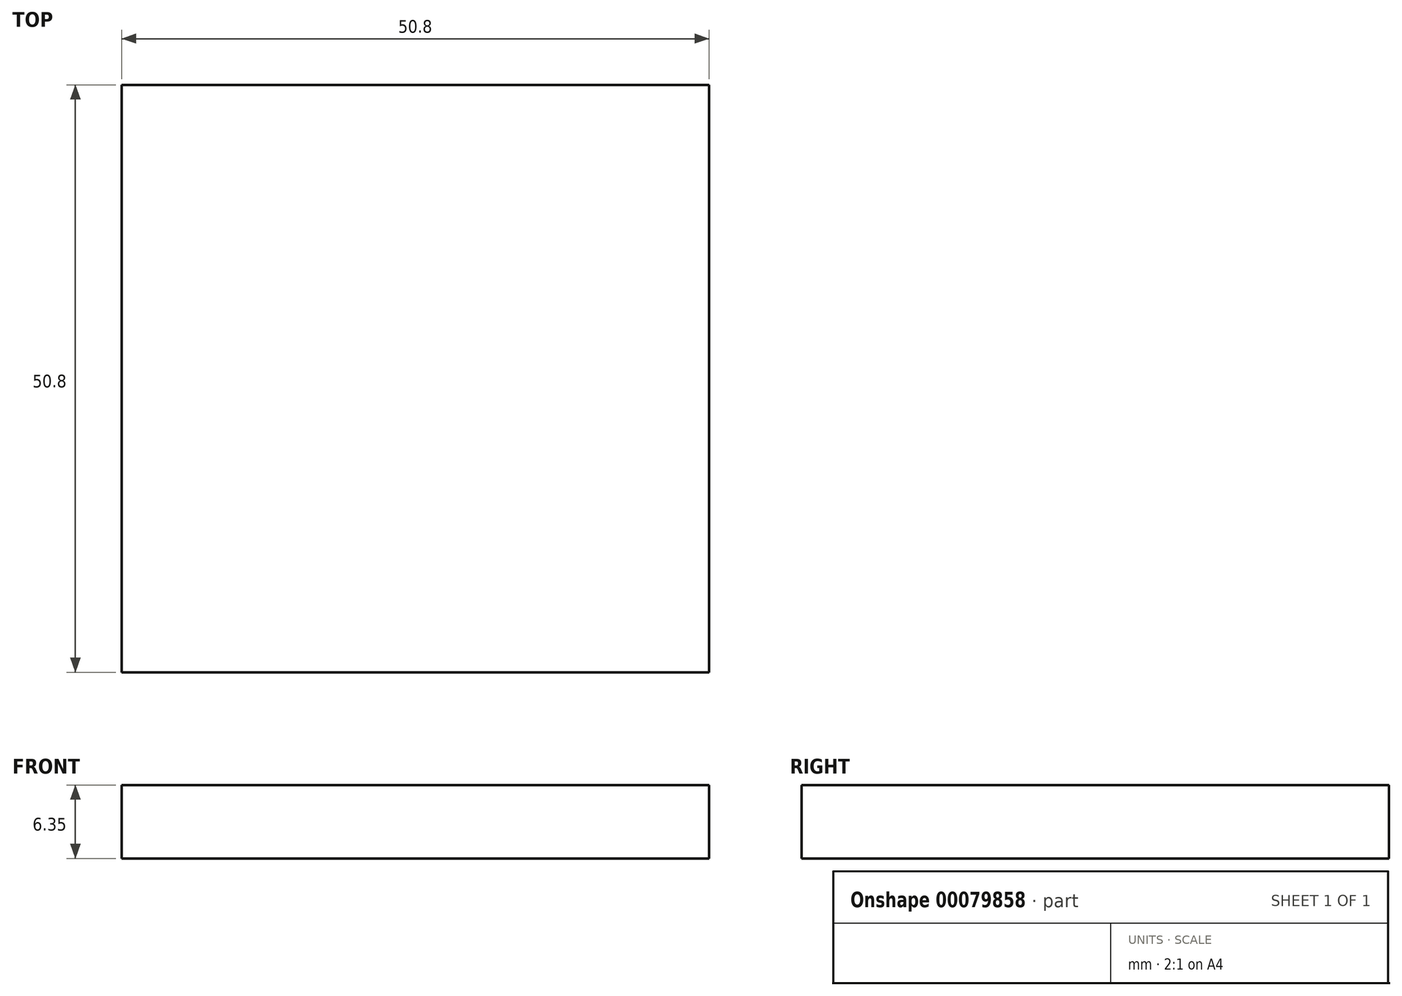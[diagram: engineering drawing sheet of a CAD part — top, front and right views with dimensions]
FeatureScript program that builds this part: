
annotation { "Feature Type Name" : "Feature", "Feature Type Description" : "" }
export const myFeature = defineFeature(function(context is Context, id is Id, definition is map)
    precondition{}
    {
        {
            var Q0;
            Q0=qCreatedBy(makeId("Top.planeOp"),FACE);
            var sketch = newSketch(context, id + "F0", { "sketchPlane" : qUnion([Q0])});
            skLineSegment(sketch, "E0.bottom", {"start": v(-25.4, 25.4) * mm, "end": v(25.4, 25.4) * mm});
            skLineSegment(sketch, "E0.top", {"start": v(-25.4, -25.4) * mm, "end": v(25.4, -25.4) * mm});
            skLineSegment(sketch, "E0.left", {"start": v(-25.4, 25.4) * mm, "end": v(-25.4, -25.4) * mm});
            skLineSegment(sketch, "E0.right", {"start": v(25.4, 25.4) * mm, "end": v(25.4, -25.4) * mm});
            skPoint(sketch, "E0.middle", {"position": v(0, 0) * mm});
            skSolve(sketch);
        }
        {
            var Q0;
            Q0=makeQuery(id+"F0.imprint","IMPRINT",FACE,{"disambiguationData":[TD([[makeQuery(id+"F0.imprint","IMPRINT",EDGE,{"derivedFrom":sQuery(id+"F0.wireOp",EDGE,"E0.bottom")}),-1.0]])]});
            extrude(context, id + "F1", {"entities" : qUnion([Q0]), "depth" : 6.35 * mm});
        }
    });
